# Revit family: Drain_Pump_Series
name_source: partatom
category: Mechanical Equipment
revit_build: Autodesk Revit 2013 (Build: 20120221_2030(x64)
units: mm (PartAtom-declared; Revit-internal decimal feet)

## types (7) — shared parameters
Assembly Code = D2010900
Cord Type = UL listed, 3-wire neoprene cord and plug
Default Elevation = 0"
Description = Drain Pumps for Residential Remodeling
Discharge Diameter = 1 1/2" NPT
Discharge Radius = 3/4"
Height = 12 1/2"
Hertz = 60
Inlet Radius = 3/4"
Installation Type = Floor Mounted
Insulation = Class B
Lead Wires Insulation = Class B
Manufacturer = Zoeller
Masterformat Number = 33 36 16
Masterformat Title = Utility Septic Tank Effluent Pumps
Material = Plastic-Zoeller-Polypropylene
Max. Diameter = 14 1/2"
Motor Thermal Shutoff = Auto Reset Thermal Overload
Omniclass Table 23 Code = 23.60.30.21
Omniclass Table 23 Title = Pumps
Operation = Automatic
Phase = 1 Ph
Price = Prices may vary. Please consult Manufacturer Representative for most up-to-date price list.
Product Page URL = htthttp://www.zoellerpumps.com
Type Comments = Available in single or double seal designs.
URL = http://www.zoellerpumps.com
Vent Radius = 1"
Voltage = 115 V
Warranty Information = 36 Months (Limited)
Waste Connection = Yes

## per-type parameters (varying)
| type | Amps | Apparent Load | Cord Length | Flow @ 5' | Max. Water Temp. | Maximum Head | Model | Motor | RPM | Shipping Weight | Solid Handling | Type |
| 104-115V 1Ph | 3 A | 357 VA | 108" | 38 GPM | 110 °F | 216" | 104 | .3 HP | 3400 RPM | 19 lbs. | 3/8" Spherical Solids | Permanent Split Capacitor |
| 132-115V 1Ph | 3 A | 357 VA | 108" | 38 GPM | 110 °F | 216" | 132 | .3 HP | 3400 RPM | 19 lbs. | 3/8" Spherical Solids | Permanent Split Capacitor |
| 131-115V 1Ph | 9 A | 1081 VA | 180" | 72 GPM | 130 °F | 276" | 131 | .5 HP | 1725 RPM | 47 lbs. | 1/2" Spherical Solids | Permanent Split Capacitor |
| 105-115V 1Ph | 10 A | 1116 VA | 108" | 43 GPM | 130 °F | 231" | 105 | .3 HP | 1550 RPM | 30 lbs. | 1/2" Spherical Solids | Shaded Pole |
| 110-115V 1Ph | 10 A | 1116 VA | 108" | 43 GPM | 130 °F | 231" | 110 | .3 HP | 1550 RPM | 33 lbs. | 1/2" Spherical Solids | Shaded Pole |
| 115-115V 1Ph | 10 A | 1116 VA | 108" | 43 GPM | 130 °F | 231" | 115 | .3 HP | 1550 RPM | 35 lbs. | 1/2" Spherical Solids | Shaded Pole |
| 120-115V 1Ph | 10 A | 116 VA | 108" | 43 GPM | 130 °F | 231" | 120 | .3 HP | 1550 RPM | 38 lbs. | 1/2" Spherical Solids | Shaded Pole |

## geometry (parser evidence)
native form markers: Blend x10, Sweep x3
no freeform markers — native parametric forms only
